# Revit family: 20200130_Monkeytoe_Purlin Mounted Platform
name_source: partatom
category: Modelos genéricos
revit_build: Autodesk Revit 2017 (Build: 20160225_1515(x64)
units: mm (PartAtom-declared; Revit-internal decimal feet)

## family parameters
Anfitrión = Cubierta
Compartido = No
Corte con vacíos al cargar = No
Cota de conector redondo = Diámetro de uso
Puede alojar armadura = No
Punto de cálculo de habitación = No
Siempre vertical = Sí
Tipo de pieza = Normal

## types (21) — shared parameters
1200mm Max. Truss Spacing (1) = No
1200mm Purlin Centers (2) = Sí
1200mm Purlin Centers Wind Load Capacity = 4.00 kN/m²
1200mm Screen Support Spacing (2) = Sí
1500 Screen Height (1) = No
1500mm Truss Mounted Screen Height (1) = Sí
1800 Screen Height (2) = Sí
1800mm Screen Support Spacing (3) = No
1800mm Truss Mounted Screen Height (2) = No
2000mm Max. Truss Spacing (2) = Sí
2400 Screen Height (3) = No
2400mm Max. Truss Spacing (3) = No
2400mm Truss Mounted Screen Height (3) = No
3000 Screen Height (4) = No
3000mm Truss Mounted Screen Height (4) = No
600mm Screen Support Spacing (1) = No
900mm Purlin Centers (1) = No
900mm Purlin Centers Wind Load Capacity = 4.00 kN/m²
Acoustic Screening Only_A (3) = No
Acoustic Screening Only_B (3) = No
Acoustic Screening Only_C (3) = No
Fabricante = Monkeytoe
Handrail_A (5) = No
Handrail_B (5) = No
Handrail_C (5) = No
Handrail_D (2) = No
Louvres and Acoustic Screening_A (2) = No
Louvres and Acoustic Screening_B (2) = No
Louvres and Acoustic Screening_C (2) = No
Louvres_A (1) = Sí
Louvres_B (1) = Sí
Louvres_C (1) = Sí
Max. Imposed Live Load = 3.00 kN/m²
Max. Length = 60000 mm  [stored 196.85 ft]
Max. Truss Spacing = 2000 mm  [stored 6.56168 ft]
Min. - Max. Purlin Centers = 2
Min. - Max. Screen Height = 2
Min. - Max. Screen Support Spacing = 2
Min. - Max. Select Screen Options Side A = 1
Min. - Max. Select Screen Options Side B = 1
Min. - Max. Select Screen Options Side C = 1
Min. - Max. Select Screen Options Side D = 1
Min. - Max. Truss Mounted Screen Height = 1
Min. - Max. Truss Spacing = 2
Perforated Sheet Screens_A (4) = No
Perforated Sheet Screens_B (4) = No
Perforated Sheet Screens_C (4) = No
Real Max. Truss Spacing = 2000 mm  [stored 6.56168 ft]
Real Purlin Centers = 1200 mm
Real Screen Height = 1800 mm  [stored 5.90551 ft]
Real Screen Support Spacing = 1200 mm
Real Truss Mounted Screen Height = 1500 mm  [stored 4.92126 ft]
Real Truss Spacing = 2000 mm  [stored 6.56168 ft]
Screen Height = 1800 mm  [stored 5.90551 ft]
Screen Support Spacing = 1200 mm
Screen Supports Wind Load Capacity = 4.00 kN/m²
Select Max. Truss Spacing = 2
Select Purlin Centers = 2
Select Screen Height = 2
Select Screen Options Side A = 1
Select Screen Options Side B = 1
Select Screen Options Side C = 1
Select Screen Support Spacing = 2
Select Truss Mounted Screen Height = 1
Truss Mounted Screen Height = 1500 mm  [stored 4.92126 ft]
URL = https://www.monkeytoe.co.nz

## per-type parameters (varying)
| type | Depth Platform | Height Platform | Length Platform | Louvres_D (1) | MT_001 | Max. Depth | N° Panel Platform | N° Purlin Platform | N° Truss | N° Truss_Step 1 | Rail_Lenght | Real Depth Platform | Real Depth Step 1 | Real Depth Step 2 | Real Height Platform | Real Height Platform Step 1 | Real Length Platform | Real Length Step 1 | Real Length Step 2 | Roof Pitch | Select Screen Options Side D | Side Distance Truss | Side Distance Truss_Step 1 | Truss Spacing |
| Platform Standard Size - 0° Depth 14.4m | 6000 mm  [stored 19.685 ft] | 500 mm  [stored 1.64042 ft] | 4200 mm  [stored 13.7795 ft] | No | MT_001 | 14400 mm  [stored 47.2441 ft] | 7 | 12 | 3 | 3 | 1700 mm | 6000 mm  [stored 19.685 ft] | 6000 mm  [stored 19.685 ft] | 6000 mm  [stored 19.685 ft] | 500 mm  [stored 1.64042 ft] | 500 mm  [stored 1.64042 ft] | 4200 mm  [stored 13.7795 ft] | 4200 mm  [stored 13.7795 ft] | 4200 mm  [stored 13.7795 ft] | 0.40° | 0 | 100 mm  [stored 0.328084 ft] | 100 mm  [stored 0.328084 ft] | 2400 mm  [stored 7.87402 ft] |
| Platform Standard Size - 01° Depth 14.4m | 14400 mm  [stored 47.2441 ft] | 500 mm  [stored 1.64042 ft] | 4200 mm  [stored 13.7795 ft] | No | MT_001 | 14400 mm  [stored 47.2441 ft] | 7 | 26 | 3 | 3 | 1700 mm | 14400 mm  [stored 47.2441 ft] | 14400 mm  [stored 47.2441 ft] | 14400 mm  [stored 47.2441 ft] | 500 mm  [stored 1.64042 ft] | 500 mm  [stored 1.64042 ft] | 4200 mm  [stored 13.7795 ft] | 4200 mm  [stored 13.7795 ft] | 4200 mm  [stored 13.7795 ft] | 1.00° | 0 | 100 mm  [stored 0.328084 ft] | 100 mm  [stored 0.328084 ft] | 2400 mm  [stored 7.87402 ft] |
| Platform Standard Size - 02° Depth 14.4m | 6000 mm  [stored 19.685 ft] | 500 mm  [stored 1.64042 ft] | 4200 mm  [stored 13.7795 ft] | No | <Por categoría> | 14400 mm  [stored 47.2441 ft] | 7 | 12 | 3 | 3 | 1700 mm | 6000 mm  [stored 19.685 ft] | 6000 mm  [stored 19.685 ft] | 6000 mm  [stored 19.685 ft] | 500 mm  [stored 1.64042 ft] | 500 mm  [stored 1.64042 ft] | 4200 mm  [stored 13.7795 ft] | 4200 mm  [stored 13.7795 ft] | 4200 mm  [stored 13.7795 ft] | 2.00° | 0 | 100 mm  [stored 0.328084 ft] | 100 mm  [stored 0.328084 ft] | 2400 mm  [stored 7.87402 ft] |
| Platform Standard Size - 03° Depth 14.4m | 6000 mm  [stored 19.685 ft] | 500 mm  [stored 1.64042 ft] | 4200 mm  [stored 13.7795 ft] | No | MT_001 | 14400 mm  [stored 47.2441 ft] | 7 | 12 | 3 | 3 | 1700 mm | 6000 mm  [stored 19.685 ft] | 6000 mm  [stored 19.685 ft] | 6000 mm  [stored 19.685 ft] | 500 mm  [stored 1.64042 ft] | 500 mm  [stored 1.64042 ft] | 4200 mm  [stored 13.7795 ft] | 4200 mm  [stored 13.7795 ft] | 4200 mm  [stored 13.7795 ft] | 3.00° | 0 | 100 mm  [stored 0.328084 ft] | 100 mm  [stored 0.328084 ft] | 2400 mm  [stored 7.87402 ft] |
| Platform Standard Size - 05° Depth 10.2m | 10200 mm  [stored 33.4646 ft] | 500 mm  [stored 1.64042 ft] | 4200 mm  [stored 13.7795 ft] | No | MT_001 | 10200 mm  [stored 33.4646 ft] | 7 | 19 | 3 | 3 | 1700 mm | 10200 mm  [stored 33.4646 ft] | 10200 mm  [stored 33.4646 ft] | 10200 mm  [stored 33.4646 ft] | 500 mm  [stored 1.64042 ft] | 500 mm  [stored 1.64042 ft] | 4200 mm  [stored 13.7795 ft] | 4200 mm  [stored 13.7795 ft] | 4200 mm  [stored 13.7795 ft] | 5.00° | 0 | 100 mm  [stored 0.328084 ft] | 100 mm  [stored 0.328084 ft] | 2400 mm  [stored 7.87402 ft] |
| Platform Standard Size - 04° Depth 13.2m | 6000 mm  [stored 19.685 ft] | 500 mm  [stored 1.64042 ft] | 4200 mm  [stored 13.7795 ft] | No | MT_001 | 13200 mm  [stored 43.3071 ft] | 7 | 12 | 3 | 3 | 1700 mm | 6000 mm  [stored 19.685 ft] | 6000 mm  [stored 19.685 ft] | 6000 mm  [stored 19.685 ft] | 500 mm  [stored 1.64042 ft] | 500 mm  [stored 1.64042 ft] | 4200 mm  [stored 13.7795 ft] | 4200 mm  [stored 13.7795 ft] | 4200 mm  [stored 13.7795 ft] | 4.00° | 0 | 100 mm  [stored 0.328084 ft] | 100 mm  [stored 0.328084 ft] | 2400 mm  [stored 7.87402 ft] |
| Platform Standard Size - 06° Depth 9m | 9000 mm  [stored 29.5276 ft] | 500 mm  [stored 1.64042 ft] | 4200 mm  [stored 13.7795 ft] | No | MT_001 | 9000 mm  [stored 29.5276 ft] | 7 | 17 | 3 | 3 | 1700 mm | 9000 mm  [stored 29.5276 ft] | 9000 mm  [stored 29.5276 ft] | 9000 mm  [stored 29.5276 ft] | 500 mm  [stored 1.64042 ft] | 500 mm  [stored 1.64042 ft] | 4200 mm  [stored 13.7795 ft] | 4200 mm  [stored 13.7795 ft] | 4200 mm  [stored 13.7795 ft] | 6.00° | 0 | 100 mm  [stored 0.328084 ft] | 100 mm  [stored 0.328084 ft] | 2400 mm  [stored 7.87402 ft] |
| Platform Standard Size - 07° Depth 7.8m | 7800 mm  [stored 25.5906 ft] | 500 mm  [stored 1.64042 ft] | 4200 mm  [stored 13.7795 ft] | No | MT_001 | 7800 mm  [stored 25.5906 ft] | 7 | 15 | 3 | 3 | 1700 mm | 7800 mm  [stored 25.5906 ft] | 7800 mm  [stored 25.5906 ft] | 7800 mm  [stored 25.5906 ft] | 500 mm  [stored 1.64042 ft] | 500 mm  [stored 1.64042 ft] | 4200 mm  [stored 13.7795 ft] | 4200 mm  [stored 13.7795 ft] | 4200 mm  [stored 13.7795 ft] | 7.00° | 0 | 100 mm  [stored 0.328084 ft] | 100 mm  [stored 0.328084 ft] | 2400 mm  [stored 7.87402 ft] |
| Platform Standard Size - 08° Depth 6m | 6000 mm  [stored 19.685 ft] | 500 mm  [stored 1.64042 ft] | 4200 mm  [stored 13.7795 ft] | No | MT_001 | 6000 mm  [stored 19.685 ft] | 7 | 12 | 3 | 3 | 1700 mm | 6000 mm  [stored 19.685 ft] | 6000 mm  [stored 19.685 ft] | 6000 mm  [stored 19.685 ft] | 500 mm  [stored 1.64042 ft] | 500 mm  [stored 1.64042 ft] | 4200 mm  [stored 13.7795 ft] | 4200 mm  [stored 13.7795 ft] | 4200 mm  [stored 13.7795 ft] | 8.00° | 0 | 100 mm  [stored 0.328084 ft] | 100 mm  [stored 0.328084 ft] | 2400 mm  [stored 7.87402 ft] |
| Platform Standard Size - 09° Depth 5.4m | 5400 mm  [stored 17.7165 ft] | 500 mm  [stored 1.64042 ft] | 4200 mm  [stored 13.7795 ft] | No | MT_001 | 5400 mm  [stored 17.7165 ft] | 7 | 10 | 3 | 3 | 1700 mm | 5400 mm  [stored 17.7165 ft] | 5400 mm  [stored 17.7165 ft] | 5400 mm  [stored 17.7165 ft] | 500 mm  [stored 1.64042 ft] | 500 mm  [stored 1.64042 ft] | 4200 mm  [stored 13.7795 ft] | 4200 mm  [stored 13.7795 ft] | 4200 mm  [stored 13.7795 ft] | 9.00° | 0 | 100 mm  [stored 0.328084 ft] | 100 mm  [stored 0.328084 ft] | 2400 mm  [stored 7.87402 ft] |
| Platform Standard Size - 10° Depth 5.4m | 5400 mm  [stored 17.7165 ft] | 500 mm  [stored 1.64042 ft] | 4200 mm  [stored 13.7795 ft] | No | MT_001 | 5400 mm  [stored 17.7165 ft] | 7 | 10 | 3 | 3 | 1700 mm | 5400 mm  [stored 17.7165 ft] | 5400 mm  [stored 17.7165 ft] | 5400 mm  [stored 17.7165 ft] | 500 mm  [stored 1.64042 ft] | 500 mm  [stored 1.64042 ft] | 4200 mm  [stored 13.7795 ft] | 4200 mm  [stored 13.7795 ft] | 4200 mm  [stored 13.7795 ft] | 10.00° | 0 | 100 mm  [stored 0.328084 ft] | 100 mm  [stored 0.328084 ft] | 2400 mm  [stored 7.87402 ft] |
| Platform Standard Size - 11° Depth 4.8m | 4800 mm | 500 mm  [stored 1.64042 ft] | 4200 mm  [stored 13.7795 ft] | No | MT_001 | 4800 mm | 7 | 9 | 3 | 3 | 1700 mm | 4800 mm | 4800 mm | 4800 mm | 500 mm  [stored 1.64042 ft] | 500 mm  [stored 1.64042 ft] | 4200 mm  [stored 13.7795 ft] | 4200 mm  [stored 13.7795 ft] | 4200 mm  [stored 13.7795 ft] | 11.00° | 0 | 100 mm  [stored 0.328084 ft] | 100 mm  [stored 0.328084 ft] | 2400 mm  [stored 7.87402 ft] |
| Platform Standard Size - 12° Depth 4.2m | 4200 mm  [stored 13.7795 ft] | 500 mm  [stored 1.64042 ft] | 4200 mm  [stored 13.7795 ft] | No | MT_001 | 4200 mm  [stored 13.7795 ft] | 7 | 8 | 3 | 3 | 1700 mm | 4200 mm  [stored 13.7795 ft] | 4200 mm  [stored 13.7795 ft] | 4200 mm  [stored 13.7795 ft] | 500 mm  [stored 1.64042 ft] | 500 mm  [stored 1.64042 ft] | 4200 mm  [stored 13.7795 ft] | 4200 mm  [stored 13.7795 ft] | 4200 mm  [stored 13.7795 ft] | 12.00° | 0 | 100 mm  [stored 0.328084 ft] | 100 mm  [stored 0.328084 ft] | 2400 mm  [stored 7.87402 ft] |
| Platform Standard Size - 13° Depth 4.2m | 4200 mm  [stored 13.7795 ft] | 500 mm  [stored 1.64042 ft] | 4200 mm  [stored 13.7795 ft] | No | MT_001 | 4200 mm  [stored 13.7795 ft] | 7 | 8 | 3 | 3 | 1700 mm | 4200 mm  [stored 13.7795 ft] | 4200 mm  [stored 13.7795 ft] | 4200 mm  [stored 13.7795 ft] | 500 mm  [stored 1.64042 ft] | 500 mm  [stored 1.64042 ft] | 4200 mm  [stored 13.7795 ft] | 4200 mm  [stored 13.7795 ft] | 4200 mm  [stored 13.7795 ft] | 13.00° | 0 | 100 mm  [stored 0.328084 ft] | 100 mm  [stored 0.328084 ft] | 2400 mm  [stored 7.87402 ft] |
| Platform Standard Size - 14° Depth 4.2m | 4200 mm  [stored 13.7795 ft] | 500 mm  [stored 1.64042 ft] | 4200 mm  [stored 13.7795 ft] | No | MT_001 | 4200 mm  [stored 13.7795 ft] | 7 | 8 | 3 | 3 | 1700 mm | 4200 mm  [stored 13.7795 ft] | 4200 mm  [stored 13.7795 ft] | 4200 mm  [stored 13.7795 ft] | 500 mm  [stored 1.64042 ft] | 500 mm  [stored 1.64042 ft] | 4200 mm  [stored 13.7795 ft] | 4200 mm  [stored 13.7795 ft] | 4200 mm  [stored 13.7795 ft] | 14.00° | 0 | 100 mm  [stored 0.328084 ft] | 100 mm  [stored 0.328084 ft] | 2400 mm  [stored 7.87402 ft] |
| Platform Standard Size - 15° Depth 3.6m | 3600 mm  [stored 11.811 ft] | 500 mm  [stored 1.64042 ft] | 6000 mm  [stored 19.685 ft] | No | MT_001 | 3600 mm  [stored 11.811 ft] | 10 | 7 | 4 | 4 | 2600 mm | 3600 mm  [stored 11.811 ft] | 3600 mm  [stored 11.811 ft] | 3600 mm  [stored 11.811 ft] | 500 mm  [stored 1.64042 ft] | 500 mm  [stored 1.64042 ft] | 6000 mm  [stored 19.685 ft] | 6000 mm  [stored 19.685 ft] | 6000 mm  [stored 19.685 ft] | 15.00° | 0 | 0 mm  [stored 0 ft] | 0 mm  [stored 0 ft] | 2400 mm  [stored 7.87402 ft] |
| Platform Standard Size - 16° Depth 3.6m | 3600 mm  [stored 11.811 ft] | 500 mm  [stored 1.64042 ft] | 4200 mm  [stored 13.7795 ft] | No | MT_001 | 3600 mm  [stored 11.811 ft] | 7 | 7 | 3 | 3 | 1700 mm | 3600 mm  [stored 11.811 ft] | 3600 mm  [stored 11.811 ft] | 3600 mm  [stored 11.811 ft] | 500 mm  [stored 1.64042 ft] | 500 mm  [stored 1.64042 ft] | 4200 mm  [stored 13.7795 ft] | 4200 mm  [stored 13.7795 ft] | 4200 mm  [stored 13.7795 ft] | 16.00° | 0 | 100 mm  [stored 0.328084 ft] | 100 mm  [stored 0.328084 ft] | 2400 mm  [stored 7.87402 ft] |
| Platform Standard Size - 17° Depth 3.6m | 3600 mm  [stored 11.811 ft] | 500 mm  [stored 1.64042 ft] | 4200 mm  [stored 13.7795 ft] | No | MT_001 | 3600 mm  [stored 11.811 ft] | 7 | 7 | 3 | 3 | 1700 mm | 3600 mm  [stored 11.811 ft] | 3600 mm  [stored 11.811 ft] | 3600 mm  [stored 11.811 ft] | 500 mm  [stored 1.64042 ft] | 500 mm  [stored 1.64042 ft] | 4200 mm  [stored 13.7795 ft] | 4200 mm  [stored 13.7795 ft] | 4200 mm  [stored 13.7795 ft] | 17.00° | 0 | 100 mm  [stored 0.328084 ft] | 100 mm  [stored 0.328084 ft] | 2400 mm  [stored 7.87402 ft] |
| Platform Standard Size - 18° Depth 3m | 4200 mm  [stored 13.7795 ft] | 500 mm  [stored 1.64042 ft] | 4200 mm  [stored 13.7795 ft] | No | MT_001 | 3000 mm  [stored 9.84252 ft] | 7 | 6 | 3 | 3 | 1700 mm | 3000 mm  [stored 9.84252 ft] | 3000 mm  [stored 9.84252 ft] | 3000 mm  [stored 9.84252 ft] | 500 mm  [stored 1.64042 ft] | 500 mm  [stored 1.64042 ft] | 4200 mm  [stored 13.7795 ft] | 4200 mm  [stored 13.7795 ft] | 4200 mm  [stored 13.7795 ft] | 18.00° | 0 | 100 mm  [stored 0.328084 ft] | 100 mm  [stored 0.328084 ft] | 2400 mm  [stored 7.87402 ft] |
| Platform Standard Size - 19° Depth 2.4m | 2400 mm  [stored 7.87402 ft] | 500 mm  [stored 1.64042 ft] | 4200 mm  [stored 13.7795 ft] | No | MT_001 | 2400 mm  [stored 7.87402 ft] | 7 | 5 | 3 | 3 | 1700 mm | 2400 mm  [stored 7.87402 ft] | 2400 mm  [stored 7.87402 ft] | 2400 mm  [stored 7.87402 ft] | 500 mm  [stored 1.64042 ft] | 500 mm  [stored 1.64042 ft] | 4200 mm  [stored 13.7795 ft] | 4200 mm  [stored 13.7795 ft] | 4200 mm  [stored 13.7795 ft] | 19.00° | 0 | 100 mm  [stored 0.328084 ft] | 100 mm  [stored 0.328084 ft] | 2400 mm  [stored 7.87402 ft] |
| Platform Standard Size - 20° Depth 2.4m | 2400 mm  [stored 7.87402 ft] | 600 mm  [stored 1.9685 ft] | 4200 mm  [stored 13.7795 ft] | Sí | MT_001 | 2400 mm  [stored 7.87402 ft] | 7 | 5 | 3 | 3 | 1700 mm | 2400 mm  [stored 7.87402 ft] | 2400 mm  [stored 7.87402 ft] | 2400 mm  [stored 7.87402 ft] | 523 mm | 523 mm | 4200 mm  [stored 13.7795 ft] | 4200 mm  [stored 13.7795 ft] | 4200 mm  [stored 13.7795 ft] | 20.00° | 1 | 100 mm  [stored 0.328084 ft] | 100 mm  [stored 0.328084 ft] | 2000 mm  [stored 6.56168 ft] |

note: [stored X ft] marks values corroborated as IEEE doubles in the binary element streams (Revit-internal decimal feet)

## geometry (parser evidence)
native form markers: Sweep x311
no freeform markers — native parametric forms only
